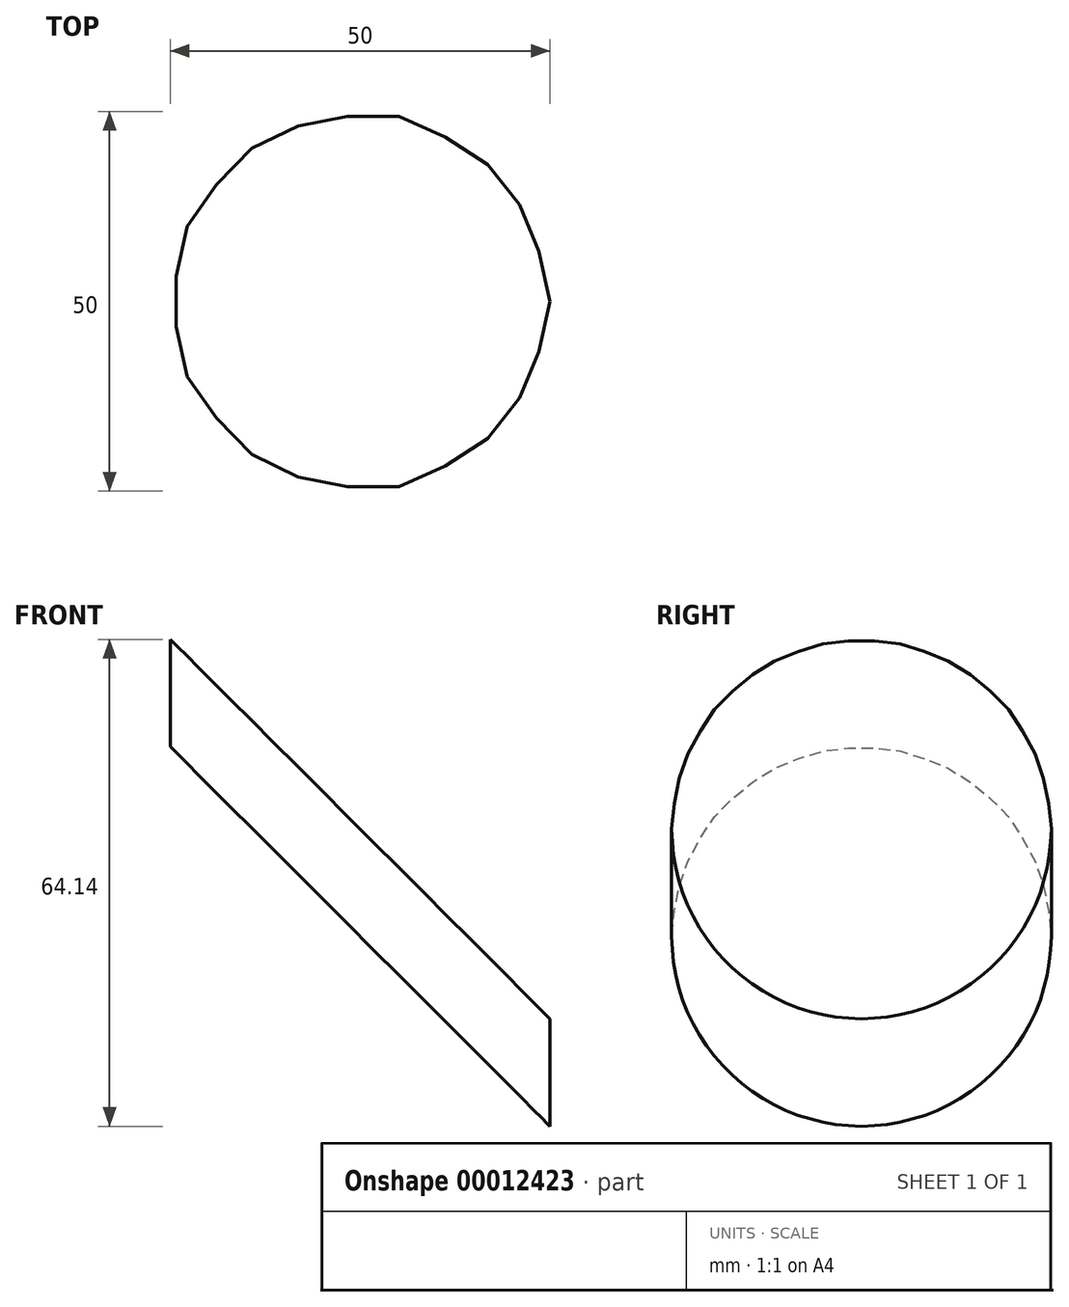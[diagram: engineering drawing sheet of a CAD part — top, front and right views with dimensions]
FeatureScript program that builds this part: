
annotation { "Feature Type Name" : "Feature", "Feature Type Description" : "" }
export const myFeature = defineFeature(function(context is Context, id is Id, definition is map)
    precondition{}
    {
        {
            var Q0;
            Q0=qCreatedBy(makeId("Top.planeOp"),FACE);
            var sketch = newSketch(context, id + "F0", { "sketchPlane" : qUnion([Q0])});
            skCircle(sketch, "E0", {"center": v(0, 0) * mm, "radius": 25 * mm});
            skSolve(sketch);
        }
        {
            var Q0;
            Q0 = qSketchRegion(id + "F0", true);
            extrude(context, id + "F1", {"entities" : qUnion([Q0]), "depth" : 64.14 * mm});
        }
        {
            var Q0;
            Q0=qCreatedBy(makeId("Front.planeOp"),FACE);
            var sketch = newSketch(context, id + "F2", { "sketchPlane" : qUnion([Q0])});
            skLineSegment(sketch, "E1.0", {"start": v(-25, 64.14) * mm, "end": v(25, 64.14) * mm});
            skLineSegment(sketch, "E2.0", {"start": v(-25, 0) * mm, "end": v(25, 0) * mm});
            skLineSegment(sketch, "E3", {"start": v(-25, 64.14) * mm, "end": v(25, 14.14) * mm});
            skLineSegment(sketch, "E4", {"start": v(25, 14.14) * mm, "end": v(25, 64.14) * mm});
            skLineSegment(sketch, "E5", {"start": v(-25, 0) * mm, "end": v(-25, 50) * mm});
            skLineSegment(sketch, "E6", {"start": v(-25, 50) * mm, "end": v(25, 0) * mm});
            skSolve(sketch);
        }
        {
            var Q0;
            Q0 = qSketchRegion(id + "F2", true);
            extrude(context, id + "F3", {"entities" : qUnion([Q0]), "operationType" : NewBodyOperationType.REMOVE, "endBound" : BoundingType.THROUGH_ALL, "oppositeDirection" : true, "depth" : 25 * mm, "hasSecondDirection" : true, "secondDirectionBound" : SecondDirectionBoundingType.THROUGH_ALL, "secondDirectionOppositeDirection" : false, "secondDirectionDepth" : 25 * mm});
        }
    });
